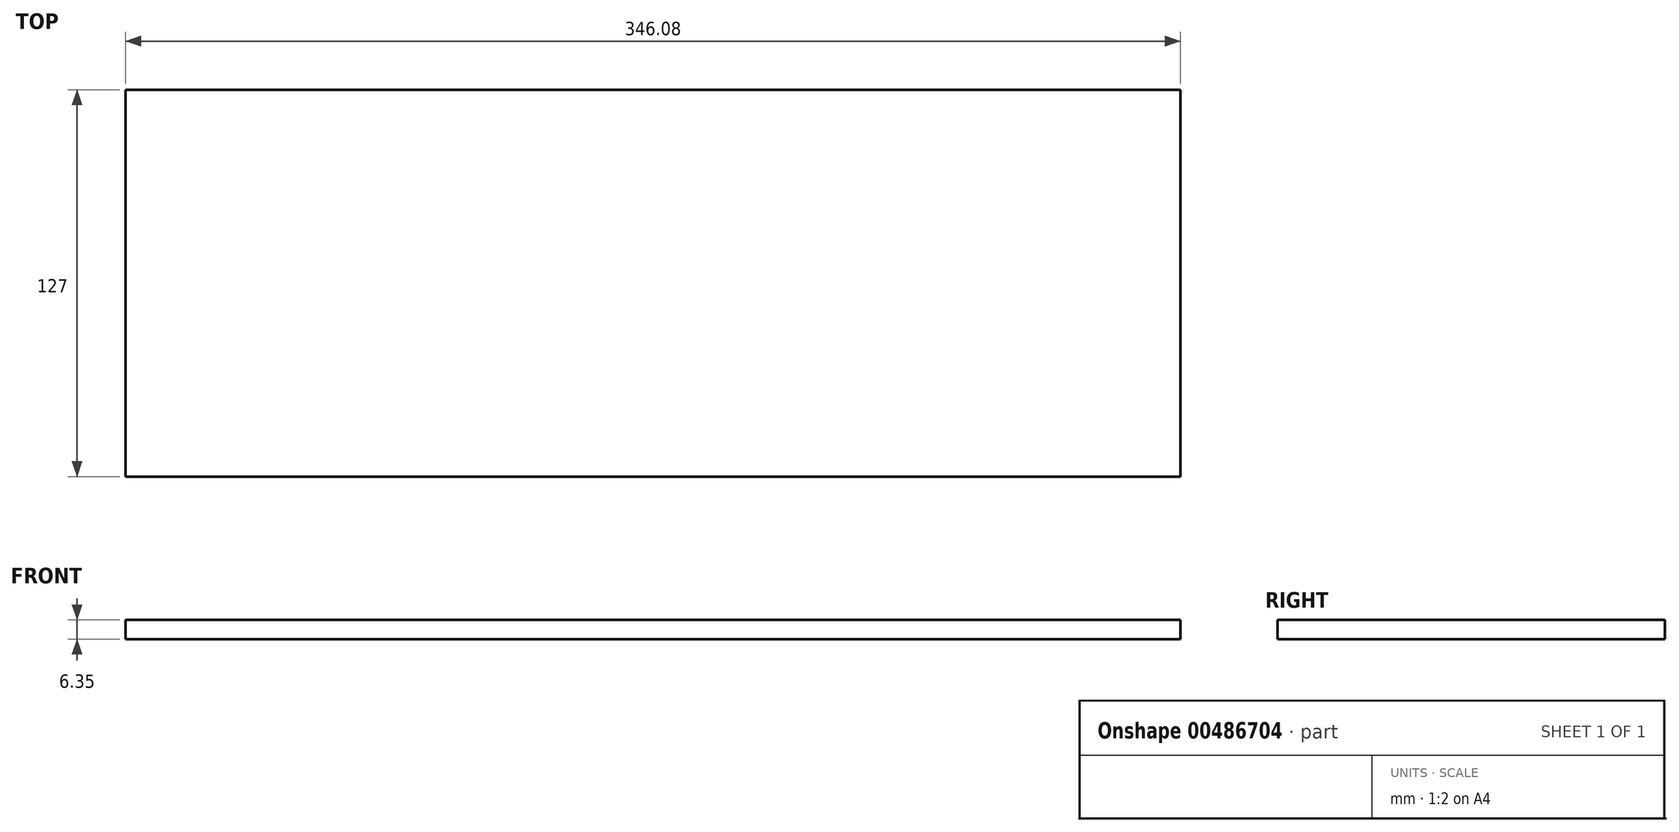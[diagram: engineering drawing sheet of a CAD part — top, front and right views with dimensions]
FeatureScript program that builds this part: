
annotation { "Feature Type Name" : "Feature", "Feature Type Description" : "" }
export const myFeature = defineFeature(function(context is Context, id is Id, definition is map)
    precondition{}
    {
        {
            var Q0;
            Q0=qCreatedBy(makeId("Top.planeOp"),FACE);
            var sketch = newSketch(context, id + "F0", { "sketchPlane" : qUnion([Q0])});
            skLineSegment(sketch, "E0.bottom", {"start": v(173.04, 63.5) * mm, "end": v(-173.04, 63.5) * mm});
            skLineSegment(sketch, "E0.top", {"start": v(173.04, -63.5) * mm, "end": v(-173.04, -63.5) * mm});
            skLineSegment(sketch, "E0.left", {"start": v(173.04, 63.5) * mm, "end": v(173.04, -63.5) * mm});
            skLineSegment(sketch, "E0.right", {"start": v(-173.04, 63.5) * mm, "end": v(-173.04, -63.5) * mm});
            skPoint(sketch, "E0.middle", {"position": v(0, 0) * mm});
            skSolve(sketch);
        }
        {
            var Q0;
            Q0 = qSketchRegion(id + "F0", true);
            extrude(context, id + "F1", {"entities" : qUnion([Q0]), "depth" : 6.35 * mm});
        }
    });
